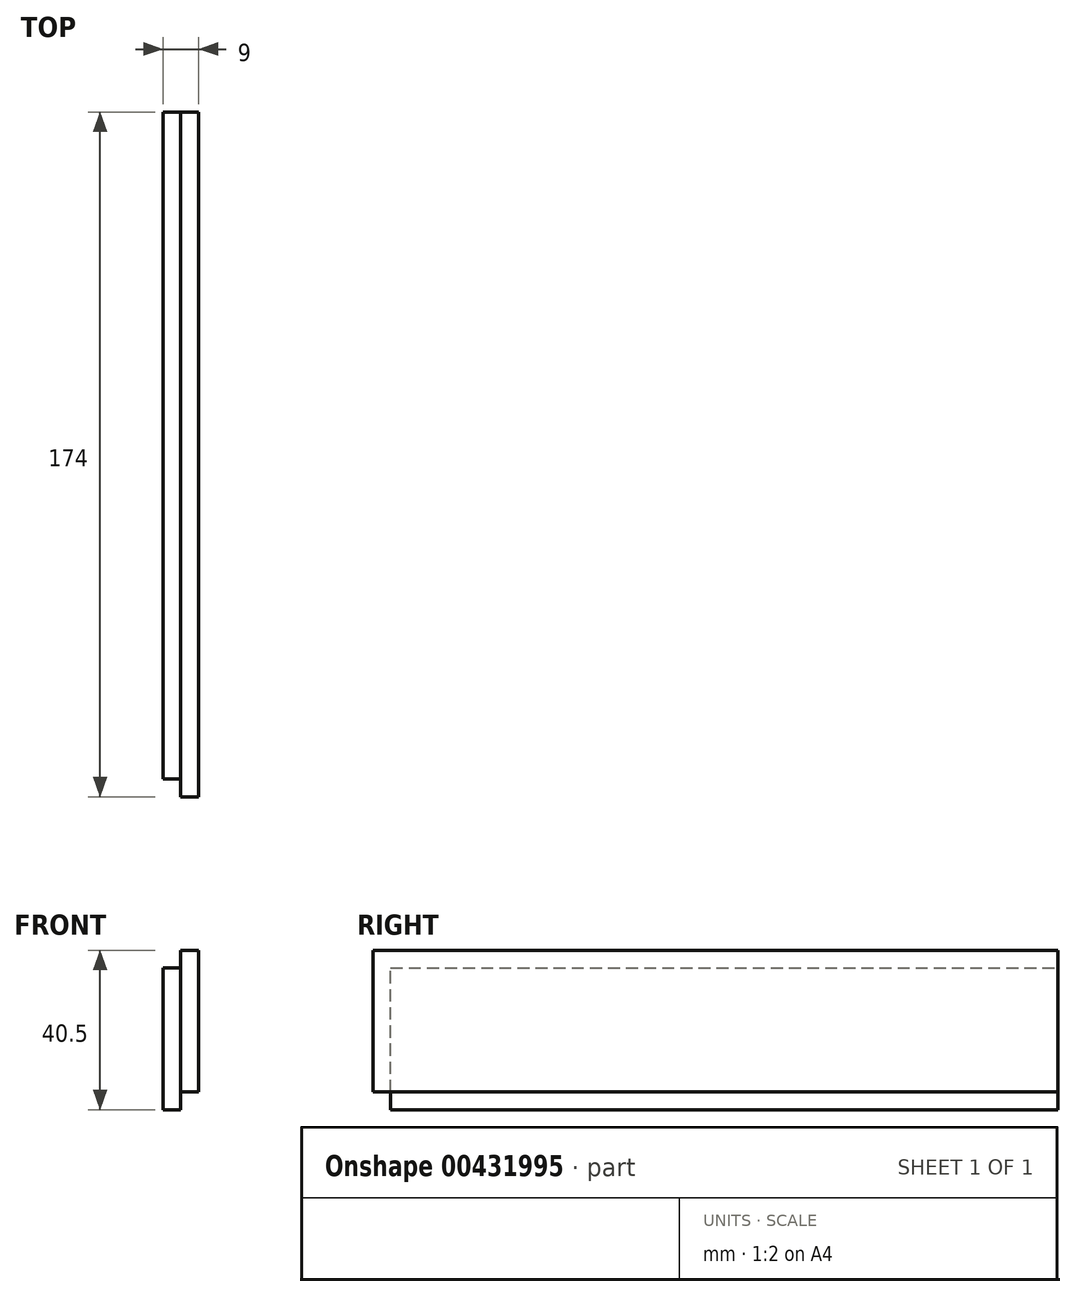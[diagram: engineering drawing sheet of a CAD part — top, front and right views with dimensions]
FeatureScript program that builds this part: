
annotation { "Feature Type Name" : "Feature", "Feature Type Description" : "" }
export const myFeature = defineFeature(function(context is Context, id is Id, definition is map)
    precondition{}
    {
        {
            var Q0;
            Q0=qCreatedBy(makeId("Right.planeOp"),FACE);
            var sketch = newSketch(context, id + "F0", { "sketchPlane" : qUnion([Q0])});
            skLineSegment(sketch, "E0.bottom", {"start": v(-87, 20.25) * mm, "end": v(87, 20.25) * mm});
            skLineSegment(sketch, "E0.top", {"start": v(-87, -20.25) * mm, "end": v(87, -20.25) * mm});
            skLineSegment(sketch, "E0.left", {"start": v(-87, 20.25) * mm, "end": v(-87, -20.25) * mm});
            skLineSegment(sketch, "E0.right", {"start": v(87, 20.25) * mm, "end": v(87, -20.25) * mm});
            skPoint(sketch, "E0.middle", {"position": v(0, 0) * mm});
            skSolve(sketch);
        }
        {
            var Q0;
            Q0=qSketchRegion(id+"F0",true);
            extrude(context, id + "F1", {"entities" : qUnion([Q0]), "depth" : 9 * mm, "offsetDistance" : 25 * mm});
        }
        {
            var Q0;
            Q0=makeQuery(id+"F1.opExtrude","SWEPT_FACE",FACE,{"disambiguationData":[OSD([sQuery(id+"F0.wireOp",EDGE,"E0.bottom")])]});
            var sketch = newSketch(context, id + "F2", { "sketchPlane" : qUnion([Q0])});
            skLineSegment(sketch, "E1.bottom", {"start": v(0, 87) * mm, "end": v(4.5, 87) * mm});
            skLineSegment(sketch, "E1.top", {"start": v(0, -87) * mm, "end": v(4.5, -87) * mm});
            skLineSegment(sketch, "E1.left", {"start": v(0, 87) * mm, "end": v(0, -87) * mm});
            skLineSegment(sketch, "E1.right", {"start": v(4.5, 87) * mm, "end": v(4.5, -87) * mm});
            skSolve(sketch);
        }
        {
            var Q0;
            Q0=qSketchRegion(id+"F2",true);
            extrude(context, id + "F3", {"entities" : qUnion([Q0]), "operationType" : NewBodyOperationType.REMOVE, "oppositeDirection" : true, "depth" : 4.5 * mm, "offsetDistance" : 25 * mm});
        }
        {
            var Q0;
            Q0=makeQuery(id+"F3.boolean.opBoolean","COPY",FACE,{"derivedFrom":makeQuery(id+"F3.opExtrude","CAP_FACE",FACE,{"disambiguationData":[OSD([sQuery(id+"F2.wireOp",EDGE,"E1.bottom"),sQuery(id+"F2.wireOp",EDGE,"E1.top"),sQuery(id+"F2.wireOp",EDGE,"E1.left"),sQuery(id+"F2.wireOp",EDGE,"E1.right")])],"isStart":false})});
            var sketch = newSketch(context, id + "F4", { "sketchPlane" : qUnion([Q0])});
            skLineSegment(sketch, "E2.bottom", {"start": v(0, -87) * mm, "end": v(4.5, -87) * mm});
            skLineSegment(sketch, "E2.top", {"start": v(0, -82.5) * mm, "end": v(4.5, -82.5) * mm});
            skLineSegment(sketch, "E2.left", {"start": v(0, -87) * mm, "end": v(0, -82.5) * mm});
            skLineSegment(sketch, "E2.right", {"start": v(4.5, -87) * mm, "end": v(4.5, -82.5) * mm});
            skSolve(sketch);
        }
        {
            var Q0;
            Q0=qSketchRegion(id+"F4",true);
            extrude(context, id + "F5", {"entities" : qUnion([Q0]), "operationType" : NewBodyOperationType.REMOVE, "endBound" : BoundingType.UP_TO_NEXT, "oppositeDirection" : true, "depth" : 6 * mm});
        }
        {
            var Q0;
            Q0=makeQuery(id+"F1.opExtrude","SWEPT_FACE",FACE,{"disambiguationData":[OSD([sQuery(id+"F0.wireOp",EDGE,"E0.top")])]});
            var sketch = newSketch(context, id + "F6", { "sketchPlane" : qUnion([Q0])});
            skLineSegment(sketch, "E3.bottom", {"start": v(9, 87) * mm, "end": v(4.5, 87) * mm});
            skLineSegment(sketch, "E3.top", {"start": v(9, 82.5) * mm, "end": v(4.5, 82.5) * mm});
            skLineSegment(sketch, "E3.left", {"start": v(9, 87) * mm, "end": v(9, 82.5) * mm});
            skLineSegment(sketch, "E3.right", {"start": v(4.5, 87) * mm, "end": v(4.5, 82.5) * mm});
            skSolve(sketch);
        }
        {
            var Q0;
            Q0=qSketchRegion(id+"F6",true);
            extrude(context, id + "F7", {"entities" : qUnion([Q0]), "operationType" : NewBodyOperationType.REMOVE, "oppositeDirection" : true, "depth" : 4.5 * mm, "offsetDistance" : 25 * mm});
        }
        {
            var Q0;
            Q0=makeQuery(id+"F1.opExtrude","SWEPT_FACE",FACE,{"disambiguationData":[OSD([sQuery(id+"F0.wireOp",EDGE,"E0.top")])]});
            var sketch = newSketch(context, id + "F8", { "sketchPlane" : qUnion([Q0])});
            skLineSegment(sketch, "E4.bottom", {"start": v(9, -87) * mm, "end": v(4.5, -87) * mm});
            skLineSegment(sketch, "E4.top", {"start": v(9, 82.5) * mm, "end": v(4.5, 82.5) * mm});
            skLineSegment(sketch, "E4.left", {"start": v(9, -87) * mm, "end": v(9, 82.5) * mm});
            skLineSegment(sketch, "E4.right", {"start": v(4.5, -87) * mm, "end": v(4.5, 82.5) * mm});
            skSolve(sketch);
        }
        {
            var Q0;
            Q0=qSketchRegion(id+"F8",true);
            extrude(context, id + "F9", {"entities" : qUnion([Q0]), "operationType" : NewBodyOperationType.REMOVE, "oppositeDirection" : true, "depth" : 4.5 * mm, "offsetDistance" : 25 * mm});
        }
    });
